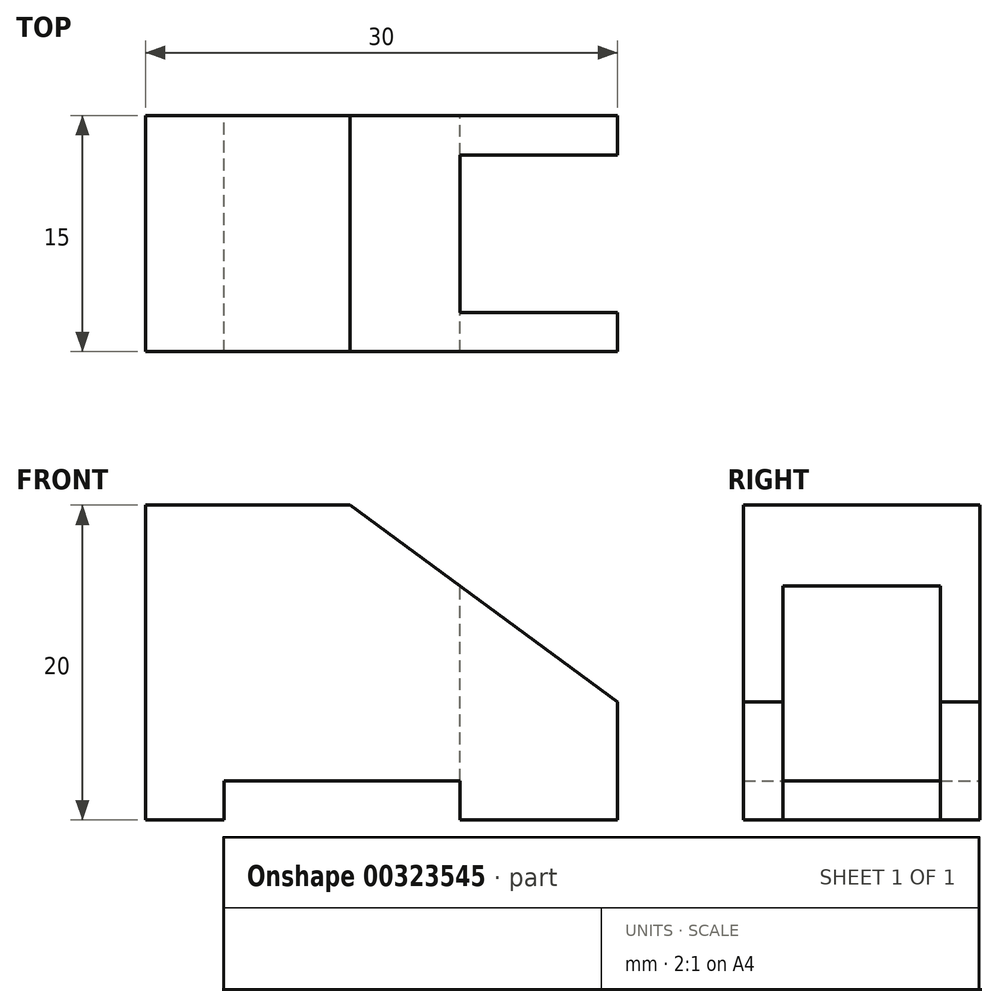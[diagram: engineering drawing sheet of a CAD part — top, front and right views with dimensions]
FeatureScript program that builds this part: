
annotation { "Feature Type Name" : "Feature", "Feature Type Description" : "" }
export const myFeature = defineFeature(function(context is Context, id is Id, definition is map)
    precondition{}
    {
        {
            var Q0;
            Q0=qCreatedBy(makeId("Front.planeOp"),FACE);
            var sketch = newSketch(context, id + "F0", { "sketchPlane" : qUnion([Q0])});
            skLineSegment(sketch, "E0.bottom", {"start": v(0, 0) * mm, "end": v(30, 0) * mm, "construction": true});
            skLineSegment(sketch, "E0.top", {"start": v(0, 20) * mm, "end": v(30, 20) * mm, "construction": true});
            skLineSegment(sketch, "E0.left", {"start": v(0, 0) * mm, "end": v(0, 20) * mm, "construction": true});
            skLineSegment(sketch, "E0.right", {"start": v(30, 0) * mm, "end": v(30, 20) * mm, "construction": true});
            skLineSegment(sketch, "E1", {"start": v(0, 0) * mm, "end": v(0, 20) * mm});
            skLineSegment(sketch, "E2", {"start": v(0, 20) * mm, "end": v(13, 20) * mm});
            skLineSegment(sketch, "E3", {"start": v(30, 7.5) * mm, "end": v(30, 0) * mm});
            skLineSegment(sketch, "E4", {"start": v(20, 0) * mm, "end": v(20, 2.5) * mm});
            skLineSegment(sketch, "E5", {"start": v(20, 2.5) * mm, "end": v(5, 2.5) * mm});
            skLineSegment(sketch, "E6", {"start": v(5, 2.5) * mm, "end": v(5, 0) * mm});
            skLineSegment(sketch, "E7", {"start": v(5, 0) * mm, "end": v(0, 0) * mm});
            skLineSegment(sketch, "E8", {"start": v(13, 20) * mm, "end": v(30, 7.5) * mm});
            skLineSegment(sketch, "E9", {"start": v(20, 0) * mm, "end": v(30, 0) * mm});
            skLineSegment(sketch, "E10", {"start": v(20, 2.5) * mm, "end": v(20, 14.85) * mm});
            skSolve(sketch);
        }
        {
            var Q0;
            Q0=makeQuery(id+"F0.imprint","IMPRINT",FACE,{"disambiguationData":[TD([[makeQuery(id+"F0.imprint","IMPRINT",EDGE,{"derivedFrom":sQuery(id+"F0.wireOp",EDGE,"E1")}),-1.0]])]});
            var Q1;
            {var subQ1=sQuery(id+"F0.wireOp",EDGE,"E3");Q1=makeQuery(id+"F0.imprint","IMPRINT",FACE,{"disambiguationData":[TD([[makeQuery(id+"F0.imprint","IMPRINT",EDGE,{"derivedFrom":subQ1}),-1.0]])]});}
            extrude(context, id + "F1", {"entities" : qUnion([Q0, Q1]), "endBound" : BoundingType.SYMMETRIC, "depth" : 15 * mm});
        }
        {
            var Q0;
            {var subQ1=sQuery(id+"F0.wireOp",EDGE,"E3");Q0=makeQuery(id+"F0.imprint","IMPRINT",FACE,{"disambiguationData":[TD([[makeQuery(id+"F0.imprint","IMPRINT",EDGE,{"derivedFrom":subQ1}),-1.0]])]});}
            extrude(context, id + "F2", {"entities" : qUnion([Q0]), "operationType" : NewBodyOperationType.REMOVE, "endBound" : BoundingType.SYMMETRIC, "oppositeDirection" : true, "depth" : 10 * mm});
        }
    });
